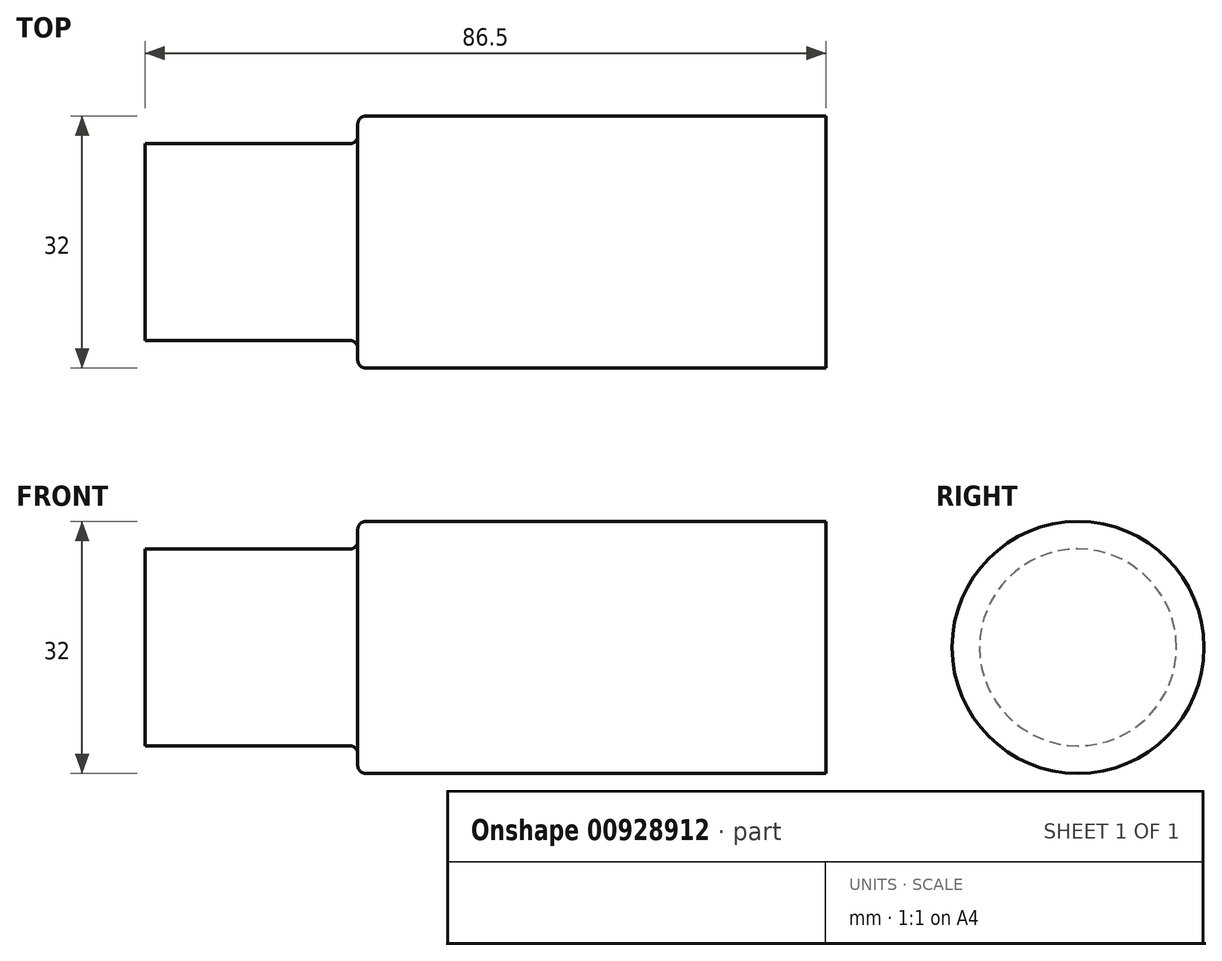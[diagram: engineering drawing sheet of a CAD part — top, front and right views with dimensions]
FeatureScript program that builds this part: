
annotation { "Feature Type Name" : "Feature", "Feature Type Description" : "" }
export const myFeature = defineFeature(function(context is Context, id is Id, definition is map)
    precondition{}
    {
        {
            var Q0;
            Q0=qCreatedBy(makeId("Front.planeOp"),FACE);
            var sketch = newSketch(context, id + "F0", { "sketchPlane" : qUnion([Q0])});
            skLineSegment(sketch, "E0", {"start": v(-38.87, 15) * mm, "end": v(-38.87, 13.5) * mm});
            skLineSegment(sketch, "E1", {"start": v(-39.87, 12.5) * mm, "end": v(-65.87, 12.5) * mm});
            skLineSegment(sketch, "E2", {"start": v(-65.87, 12.5) * mm, "end": v(-65.87, 0) * mm});
            skPoint(sketch, "E3.visualSharp", {"position": v(-38.87, 12.5) * mm});
            skArc(sketch, "E3.filletArc", {"start": v(-39.87, 12.5) * mm, "mid": v(-39.16, 12.8) * mm, "end": v(-38.87, 13.5) * mm});
            skPoint(sketch, "E4.visualSharp", {"position": v(-38.87, 16) * mm});
            skArc(sketch, "E4.filletArc", {"start": v(-37.87, 16) * mm, "mid": v(-38.57, 15.7) * mm, "end": v(-38.87, 15) * mm});
            skLineSegment(sketch, "E5", {"start": v(-65.87, 0) * mm, "end": v(20.63, 0) * mm});
            skLineSegment(sketch, "E6", {"start": v(20.63, 0) * mm, "end": v(20.63, 16) * mm});
            skLineSegment(sketch, "E7", {"start": v(20.63, 16) * mm, "end": v(-37.87, 16) * mm});
            skSolve(sketch);
        }
        {
            var Q0;
            Q0=makeQuery(id+"F0.imprint","IMPRINT",FACE,{"disambiguationData":[TD([[makeQuery(id+"F0.imprint","IMPRINT",EDGE,{"derivedFrom":sQuery(id+"F0.wireOp",EDGE,"E0")}),1.0]])]});
            var Q1;
            Q1=sQuery(id+"F0.wireOp",EDGE,"E5");
            revolve(context, id + "F1", {"surfaceOperationType" : NewSurfaceOperationType.NEW, "entities" : qUnion([Q0]), "axis" : qUnion([Q1]), "revolveType" : RevolveType.FULL});
        }
    });
